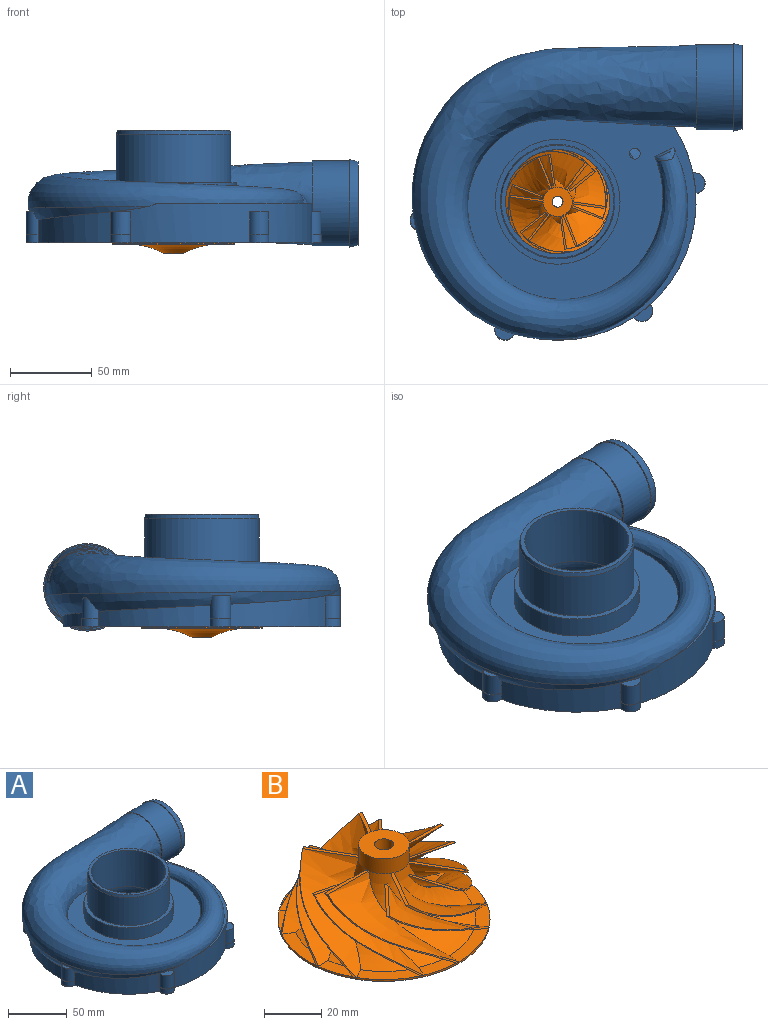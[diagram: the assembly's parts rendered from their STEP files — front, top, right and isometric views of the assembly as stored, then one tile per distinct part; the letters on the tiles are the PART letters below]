
ASSEMBLY  parts=2 mates=1
PART A: 110 faces, bbox 211.1x189.5x79.7 mm
  f0: plane 8.09x6.32mm, normal (0,0,1), area 25.7mm2, adj f11,f47,f59,f101
  f1: cylinder r=83.18mm len=70.23mm, axis (0,0,1), area 435.7mm2, adj f4,f11,f81,f99
  f2: cylinder r=84.45mm len=159.98mm, axis (0,0,1), area 4684.9mm2, adj f7,f24,f27,f28,f61,f66,f68,f72
  f3: cylinder r=83.18mm len=164.82mm, axis (0,0,1), area 4035.6mm2, adj f4,f11,f21,f32,f81,f86,f87,f90
  f4: plane 166.37x166.37mm, normal (0,0,1), area 2253.3mm2, adj f1,f3,f11,f12,f46,f47,f81,f87
  f5: plane 12.67x7.44mm, normal (0,0,1), area 3.1mm2, adj f66,f92
  f6: plane 11.52x10.42mm, normal (0,0,1), area 3.1mm2, adj f68,f88
  f7: bspline ~178.18x173.26mm, area 5206.9mm2, adj f2,f8,f10,f14,f27,f50,f61,f62
  f8: cylinder r=84.45mm len=57.92mm, axis (0,0,1), area 1246.2mm2, adj f7,f28,f70,f72,f78,f84
  f9: plane 12.31x8.98mm, normal (0,0,1), area 3.1mm2, adj f72,f84
  f10: cylinder r=84.45mm len=67.76mm, axis (0,0,1), area 858.4mm2, adj f7,f28,f64,f70,f73,f78
  f11: offset ~187.53x182.31mm, area 5116.8mm2, adj f0,f1,f3,f4,f12,f32,f37,f47
  f12: cylinder r=83.18mm len=58.91mm, axis (0,0,1), area 102.7mm2, adj f4,f11,f99
  f13: plane 12.67x7.44mm, normal (0,0,1), area 3.1mm2, adj f70,f78
  f14: cylinder r=84.45mm len=72.56mm, axis (0,0,1), area 463.3mm2, adj f7,f28,f61,f64,f73
  f15: plane 11.52x10.42mm, normal (0,0,1), area 3.1mm2, adj f64,f73
  f16: cylinder r=78.1mm len=61.64mm, axis (0,0,-1), area 414.4mm2, adj f28,f38,f69,f71
  f17: cylinder r=78.1mm len=72.11mm, axis (0,0,-1), area 414.4mm2, adj f28,f38,f63,f69
  f18: cylinder r=78.1mm len=77.22mm, axis (0,0,-1), area 414.4mm2, adj f28,f38,f67,f71
  f19: cylinder r=78.1mm len=72.11mm, axis (0,0,-1), area 414.4mm2, adj f28,f38,f65,f67
  f20: cylinder r=78.1mm len=77.22mm, axis (0,0,-1), area 414.4mm2, adj f28,f38,f60,f63
  f21: plane 139.35x134.6mm, normal (0,0,-1), area 3659mm2, adj f3,f30,f31,f32,f45,f98
  f22: cylinder r=78.1mm len=61.64mm, axis (0,0,-1), area 414.4mm2, adj f28,f38,f60,f65
  f23: plane 76.2x76.2mm, normal (0,0,1), area 728.4mm2, adj f33,f34
  f24: plane 142.95x138.21mm, normal (0,0,1), area 6867.5mm2, adj f2,f25,f26,f27,f33,f98
  f25: plane 20.05x13.89mm, normal (-0.42,0.91,0), area 17.3mm2, adj f24,f26,f29
  f26: bspline ~18.16x4.82mm, area 0.2mm2, adj f24,f25,f27
  f27: bspline ~185.39x180.67mm, area 23842.1mm2, adj f2,f7,f24,f26,f29,f50
  f28: plane 180.08x169mm, normal (0,0,-1), area 3428.3mm2, adj f2,f8,f10,f14,f16,f17,f18,f19
  f29: bspline ~11.98x8.06mm, area 54.7mm2, adj f25,f27
  f30: plane 9.84x6.94mm, normal (0.42,-0.91,0), area 54.2mm2, adj f21,f31,f32
  f31: offset ~91.68x84.15mm, area 86.2mm2, adj f21,f30,f32
  f32: offset ~187.93x183.21mm, area 22574.8mm2, adj f3,f11,f21,f30,f31,f48,f49
  f33: cylinder r=38.1mm len=76.2mm, axis (0,0,-1), area 3040.2mm2, adj f23,f24
  f34: cylinder r=34.92mm len=69.85mm, axis (0,0,-1), area 6409.8mm2, adj f23,f56
  f35: plane 68.68x68.68mm, normal (0,0,1), area 537.5mm2, adj f36,f56
  f36: cylinder r=31.75mm len=63.5mm, axis (0,0,1), area 7600.6mm2, adj f35,f44
  f37: cylinder r=83.18mm len=15.68mm, axis (0,0,-1), area 0mm2, adj f11,f47
  f38: plane 156.21x156.21mm, normal (0,0,-1), area 2702mm2, adj f16,f17,f18,f19,f20,f22,f40,f60
  f39: plane 151.13x151.13mm, normal (0,0,1), area 1475.8mm2, adj f40,f46
  f40: cylinder r=72.39mm len=144.78mm, axis (0,0,-1), area 1732.9mm2, adj f38,f39
  f41: plane 127x127mm, normal (0,0,1), area 330.1mm2, adj f43,f45
  f42: plane 127x127mm, normal (0,0,-1), area 4560.4mm2, adj f43,f44
  f43: cylinder r=63.5mm len=127mm, axis (0,0,1), area 506.7mm2, adj f41,f42
  f44: torus R=50.8mm, axis (0,0,-1), area 7271mm2, adj f36,f42
  f45: torus R=62.67mm, axis (0,0,-1), area 5832.8mm2, adj f21,f41,f96,f97
  f46: cone r=75.56mm half-angle=45deg, axis (0,0,-1), area 1734.2mm2, adj f4,f39
  f47: torus R=79.38mm, axis (0,0,-1), area 276.8mm2, adj f0,f4,f11,f37,f57,f58,f59,f101
  f48: plane 29.54x5.52mm, normal (1,0,0), area 3.1mm2, adj f11,f32,f52
  f49: plane 49.59x44.62mm, normal (-1,0,0), area 89.7mm2, adj f11,f32,f52
  f50: plane 53.49x53.48mm, normal (-1,0,0), area 115.7mm2, adj f7,f27,f51
  f51: cylinder r=25.94mm len=51.88mm, axis (-1,0,0), area 3726.1mm2, adj f50,f53
  f52: cylinder r=23.37mm len=46.74mm, axis (-1,0,0), area 4102.3mm2, adj f48,f49,f54
  f53: plane 53.34x53.34mm, normal (-1,0,0), area 120.4mm2, adj f51,f55
  f54: plane 50.99x50.99mm, normal (1,0,0), area 326.9mm2, adj f52,f55
  f55: cone r=25.5mm half-angle=13deg, axis (-1,0,0), area 854.5mm2, adj f53,f54
  f56: cone r=34.34mm half-angle=13deg, axis (0,0,-1), area 567.2mm2, adj f34,f35
  f57: plane 5.9x4.45mm, normal (0,0,1), area 12.3mm2, adj f11,f47,f58,f101
  f58: cylinder r=6.35mm len=2.95mm, axis (0,0,-1), area 1.5mm2, adj f11,f47,f57
  f59: cylinder r=6.35mm len=8.09mm, axis (0,0,-1), area 11.2mm2, adj f0,f11,f47
  f60: cylinder r=6.35mm len=5.08mm, axis (0,0,-1), area 1.1mm2, adj f20,f22,f28,f38
  f61: cylinder r=6.35mm len=12.31mm, axis (0,0,-1), area 81.2mm2, adj f2,f7,f14,f28,f62
  f62: plane 5.49x0.77mm, normal (0,0,1), area 2.3mm2, adj f7,f61
  f63: cylinder r=6.35mm len=5.08mm, axis (0,0,-1), area 1.1mm2, adj f17,f20,f28,f38
  f64: cylinder r=6.35mm len=11.52mm, axis (0,0,-1), area 103.8mm2, adj f10,f14,f15,f28
  f65: cylinder r=6.35mm len=5.08mm, axis (0,0,-1), area 1.1mm2, adj f19,f22,f28,f38
  f66: cylinder r=6.35mm len=12.67mm, axis (0,0,-1), area 103.8mm2, adj f2,f5,f28
  f67: cylinder r=6.35mm len=5.08mm, axis (0,0,-1), area 1.1mm2, adj f18,f19,f28,f38
  f68: cylinder r=6.35mm len=11.52mm, axis (0,0,-1), area 103.8mm2, adj f2,f6,f28
  f69: cylinder r=6.35mm len=5.08mm, axis (0,0,-1), area 1.1mm2, adj f16,f17,f28,f38
  f70: cylinder r=6.35mm len=12.67mm, axis (0,0,-1), area 103.8mm2, adj f8,f10,f13,f28
  f71: cylinder r=6.35mm len=5.08mm, axis (0,0,-1), area 1.1mm2, adj f16,f18,f28,f38
  f72: cylinder r=6.35mm len=12.31mm, axis (0,0,-1), area 103.8mm2, adj f2,f8,f9,f28
  f73: cylinder r=6.35mm len=13.06mm, axis (0,0,-1), area 180mm2, adj f7,f10,f14,f15
  f74: plane 11.37x10.24mm, normal (0,0,1), area 62mm2, adj f11,f75,f76,f77
  f75: cylinder r=43.48mm len=10.04mm, axis (0,0,-1), area 88.4mm2, adj f11,f74,f76,f77,f99,f100
  f76: cylinder r=6.35mm len=7.89mm, axis (0,0,-1), area 23.3mm2, adj f11,f74,f75
  f77: cylinder r=6.35mm len=8.5mm, axis (0,0,-1), area 27mm2, adj f11,f74,f75
  f78: cylinder r=6.35mm len=13.97mm, axis (0,0,-1), area 260.2mm2, adj f7,f8,f10,f13,f79
  f79: plane 10.86x4.18mm, normal (0,0,1), area 23.5mm2, adj f7,f78
  f80: plane 12.65x5.52mm, normal (0,0,1), area 47.2mm2, adj f11,f81,f82,f83
  f81: cylinder r=8.98mm len=12.7mm, axis (0,0,-1), area 123.3mm2, adj f1,f3,f4,f11,f80,f82,f83,f108
  f82: cylinder r=6.35mm len=3.04mm, axis (0,0,-1), area 2.4mm2, adj f11,f80,f81
  f83: cylinder r=6.35mm len=3.83mm, axis (0,0,-1), area 3.9mm2, adj f11,f80,f81
  f84: cylinder r=6.35mm len=13.97mm, axis (0,0,-1), area 278.5mm2, adj f2,f7,f8,f9,f85
  f85: plane 12.22x8.74mm, normal (0,0,1), area 61.2mm2, adj f2,f7,f84
  f86: plane 9.06x3.87mm, normal (0,0,1), area 10.6mm2, adj f3,f87
  f87: cylinder r=8.98mm len=12.7mm, axis (0,0,-1), area 107.5mm2, adj f3,f4,f86,f106,f107
  f88: cylinder r=6.35mm len=13.97mm, axis (0,0,-1), area 278.5mm2, adj f2,f6,f89
  f89: plane 11.37x10.23mm, normal (0,0,1), area 61.2mm2, adj f2,f88
  f90: plane 7.75x5.99mm, normal (0,0,1), area 10.6mm2, adj f3,f91
  f91: cylinder r=8.98mm len=12.7mm, axis (0,0,-1), area 107.5mm2, adj f3,f4,f90,f104,f105
  f92: cylinder r=6.35mm len=13.97mm, axis (0,0,-1), area 278.5mm2, adj f2,f5,f93
  f93: plane 12.64x7.2mm, normal (0,0,1), area 61.2mm2, adj f2,f92
  f94: plane 9.7x2.18mm, normal (0,0,1), area 10.6mm2, adj f3,f95
  f95: cylinder r=8.98mm len=12.7mm, axis (0,0,-1), area 107.1mm2, adj f3,f4,f94,f102,f103
  f96: plane 6.44x5.05mm, normal (0,0,1), area 2.9mm2, adj f45,f97
  f97: cylinder r=3.3mm len=3.84mm, axis (0,0,1), area 0mm2, adj f45,f96
  f98: cylinder r=3.3mm len=6.6mm, axis (0,0,1), area 26.3mm2, adj f21,f24
  f99: cylinder r=3.26mm len=12.7mm, axis (0,0,-1), area 208.6mm2, adj f1,f4,f11,f12,f28,f75,f100
  f100: cone r=3.26mm half-angle=59deg, axis (0,0,-1), area 24.6mm2, adj f75,f99
  f101: cylinder r=3.26mm len=6.53mm, axis (0,0,-1), area 107.2mm2, adj f0,f11,f28,f47,f57
  f102: cylinder r=3.26mm len=12.7mm, axis (0,0,-1), area 235mm2, adj f4,f28,f95,f103
  f103: cone r=3.26mm half-angle=59deg, axis (0,0,-1), area 38.2mm2, adj f95,f102
  f104: cylinder r=3.26mm len=12.7mm, axis (0,0,-1), area 235mm2, adj f4,f28,f91,f105
  f105: cone r=3.26mm half-angle=59deg, axis (0,0,-1), area 39mm2, adj f91,f104
  f106: cylinder r=3.26mm len=12.7mm, axis (0,0,-1), area 235mm2, adj f4,f28,f87,f107
  f107: cone r=3.26mm half-angle=59deg, axis (0,0,-1), area 39mm2, adj f87,f106
  f108: cylinder r=3.26mm len=12.7mm, axis (0,0,-1), area 235mm2, adj f4,f28,f81,f109
  f109: cone r=3.26mm half-angle=59deg, axis (0,0,-1), area 39mm2, adj f81,f108
PART B: 73 faces, bbox 152.8x152.6x60.1 mm
  f0: plane 74.16x74.16mm, normal (0,0,-1), area 2178.1mm2, adj f61,f72
  f1: cylinder r=8.89mm len=17.78mm, axis (0,0,-1), area 354.7mm2, adj f44,f45,f46,f47,f48,f49,f63,f65
  f2: bspline ~99.37x71.86mm, area 595.5mm2, adj f32,f39,f52,f69
  f3: bspline ~100.08x70.33mm, area 596.4mm2, adj f27,f39,f52,f69
  f4: bspline ~104.67x66.07mm, area 694.5mm2, adj f27,f44,f51,f69
  f5: bspline ~104.31x66.07mm, area 697.4mm2, adj f33,f44,f51,f68
  f6: bspline ~86.1x75.72mm, area 595.5mm2, adj f33,f40,f54,f68
  f7: bspline ~85.13x75.72mm, area 596.4mm2, adj f28,f40,f54,f68
  f8: bspline ~58.05x35.34mm, area 694.5mm2, adj f28,f45,f53,f68
  f9: bspline ~104.27x66.16mm, area 697.4mm2, adj f34,f45,f53,f67
  f10: bspline ~107.08x60.93mm, area 595.5mm2, adj f34,f41,f56,f67
  f11: bspline ~106.93x60.93mm, area 596.4mm2, adj f29,f41,f56,f67
  f12: bspline ~77.53x76.29mm, area 694.5mm2, adj f29,f46,f55,f67
  f13: bspline ~76.4x76.29mm, area 697.4mm2, adj f35,f46,f55,f66
  f14: bspline ~99.37x71.86mm, area 595.5mm2, adj f35,f42,f58,f66
  f15: bspline ~100.08x70.33mm, area 596.4mm2, adj f30,f42,f58,f66
  f16: bspline ~104.67x66.07mm, area 694.5mm2, adj f30,f47,f57,f66
  f17: bspline ~104.31x66.07mm, area 697.4mm2, adj f36,f47,f57,f65
  f18: bspline ~86.1x75.72mm, area 595.5mm2, adj f36,f43,f60,f65
  f19: bspline ~85.13x75.72mm, area 596.4mm2, adj f31,f43,f60,f65
  f20: bspline ~58.05x35.34mm, area 694.5mm2, adj f31,f48,f59,f65
  f21: bspline ~104.27x66.16mm, area 697.4mm2, adj f37,f48,f59,f70
  f22: bspline ~107.08x60.93mm, area 595.5mm2, adj f37,f38,f62,f70
  f23: bspline ~106.93x60.93mm, area 596.4mm2, adj f26,f38,f62,f70
  f24: bspline ~77.53x76.29mm, area 694.5mm2, adj f26,f49,f50,f70
  f25: bspline ~76.4x76.29mm, area 697.4mm2, adj f32,f49,f50,f69
  f26: plane 21.43x10.87mm, normal (0,0,1), area 105.6mm2, adj f23,f24,f61,f70
  f27: plane 18.69x17.51mm, normal (0,0,1), area 105.6mm2, adj f3,f4,f61,f69
  f28: plane 21.96x9.21mm, normal (0,0,1), area 105.6mm2, adj f7,f8,f61,f68
  f29: plane 21.43x10.87mm, normal (0,0,1), area 105.6mm2, adj f11,f12,f61,f67
  f30: plane 18.69x17.51mm, normal (0,0,1), area 105.6mm2, adj f15,f16,f61,f66
  f31: plane 21.96x9.21mm, normal (0,0,1), area 105.6mm2, adj f19,f20,f61,f65
  f32: plane 13.53x7.45mm, normal (0,0,1), area 63.6mm2, adj f2,f25,f61,f69
  f33: plane 13.52x8.53mm, normal (0,0,1), area 63.6mm2, adj f5,f6,f61,f68
  f34: plane 12.74x12.11mm, normal (0,0,1), area 63.6mm2, adj f9,f10,f61,f67
  f35: plane 13.53x7.45mm, normal (0,0,1), area 63.6mm2, adj f13,f14,f61,f66
  f36: plane 13.52x8.53mm, normal (0,0,1), area 63.6mm2, adj f17,f18,f61,f65
  f37: plane 12.74x12.11mm, normal (0,0,1), area 63.6mm2, adj f21,f22,f61,f70
  f38: plane 14.93x14.23mm, normal (0,0,1), area 21.2mm2, adj f22,f23,f62,f70
  f39: plane 19.23x5.58mm, normal (0,0,1), area 21.2mm2, adj f2,f3,f52,f69
  f40: plane 19.08x6.63mm, normal (0,0,1), area 21.2mm2, adj f6,f7,f54,f68
  f41: plane 14.93x14.23mm, normal (0,0,1), area 21.2mm2, adj f10,f11,f56,f67
  f42: plane 19.23x5.58mm, normal (0,0,1), area 21.2mm2, adj f14,f15,f58,f66
  f43: plane 19.08x6.63mm, normal (0,0,1), area 21.2mm2, adj f18,f19,f60,f65
  f44: plane 18.3x11.23mm, normal (0,0,1), area 25.6mm2, adj f1,f4,f5,f51
  f45: plane 18.2x11.29mm, normal (0,0,1), area 25.6mm2, adj f1,f8,f9,f53
  f46: plane 20.41x1.26mm, normal (0,0,1), area 25.6mm2, adj f1,f12,f13,f55
  f47: plane 18.3x11.23mm, normal (0,0,1), area 25.6mm2, adj f1,f16,f17,f57
  f48: plane 18.2x11.29mm, normal (0,0,1), area 25.6mm2, adj f1,f20,f21,f59
  f49: plane 20.41x1.26mm, normal (0,0,1), area 25.6mm2, adj f1,f24,f25,f50
  f50: torus R=70.62mm, axis (0,0,1), area 26.1mm2, adj f24,f25,f49,f61
  f51: torus R=70.62mm, axis (0,0,1), area 26.1mm2, adj f4,f5,f44,f61
  f52: torus R=70.62mm, axis (0,0,1), area 21.7mm2, adj f2,f3,f39,f61
  f53: torus R=70.62mm, axis (0,0,1), area 26.1mm2, adj f8,f9,f45,f61
  f54: torus R=70.62mm, axis (0,0,1), area 21.7mm2, adj f6,f7,f40,f61
  f55: torus R=70.62mm, axis (0,0,1), area 26.1mm2, adj f12,f13,f46,f61
  f56: torus R=70.62mm, axis (0,0,1), area 21.7mm2, adj f10,f11,f41,f61
  f57: torus R=70.62mm, axis (0,0,1), area 26.1mm2, adj f16,f17,f47,f61
  f58: torus R=70.62mm, axis (0,0,1), area 21.7mm2, adj f14,f15,f42,f61
  f59: torus R=70.62mm, axis (0,0,1), area 26.1mm2, adj f20,f21,f48,f61
  f60: torus R=70.62mm, axis (0,0,1), area 21.7mm2, adj f18,f19,f43,f61
  f61: cylinder r=37.08mm len=74.16mm, axis (0,0,1), area 177.5mm2, adj f0,f26,f27,f28,f29,f30,f31,f32
  f62: torus R=70.62mm, axis (0,0,1), area 21.7mm2, adj f22,f23,f38,f61
  f63: plane 17.78x17.78mm, normal (0,0,1), area 214mm2, adj f1,f64
  f64: cylinder r=3.3mm len=38.1mm, axis (0,0,1), area 790.5mm2, adj f63,f71
  f65: torus R=39.93mm, axis (0,0,1), area 620mm2, adj f1,f17,f18,f19,f20,f31,f36,f43
  f66: torus R=39.93mm, axis (0,0,1), area 620mm2, adj f1,f13,f14,f15,f16,f30,f35,f42
  f67: torus R=39.93mm, axis (0,0,1), area 620mm2, adj f1,f9,f10,f11,f12,f29,f34,f41
  f68: torus R=39.93mm, axis (0,0,1), area 620mm2, adj f1,f5,f6,f7,f8,f28,f33,f40
  f69: torus R=39.93mm, axis (0,0,1), area 620mm2, adj f1,f2,f3,f4,f25,f27,f32,f39
  f70: torus R=39.93mm, axis (0,0,1), area 620mm2, adj f1,f21,f22,f23,f24,f26,f37,f38
  f71: plane 11.94x11.94mm, normal (0,0,-1), area 77.7mm2, adj f64,f72
  f72: torus R=26.8mm, axis (0,0,1), area 2097.5mm2, adj f0,f71
PLACE A t=(0.17,0.36,-13.76)mm fixed
PLACE B rot(axis=(0,0,1),111.9deg) t=(0.17,0.36,-38.78)mm
MATE cylindrical B.f1 <-> A.f1  axis (0,0,1) through (0.17,0.36,-6.27)mm
